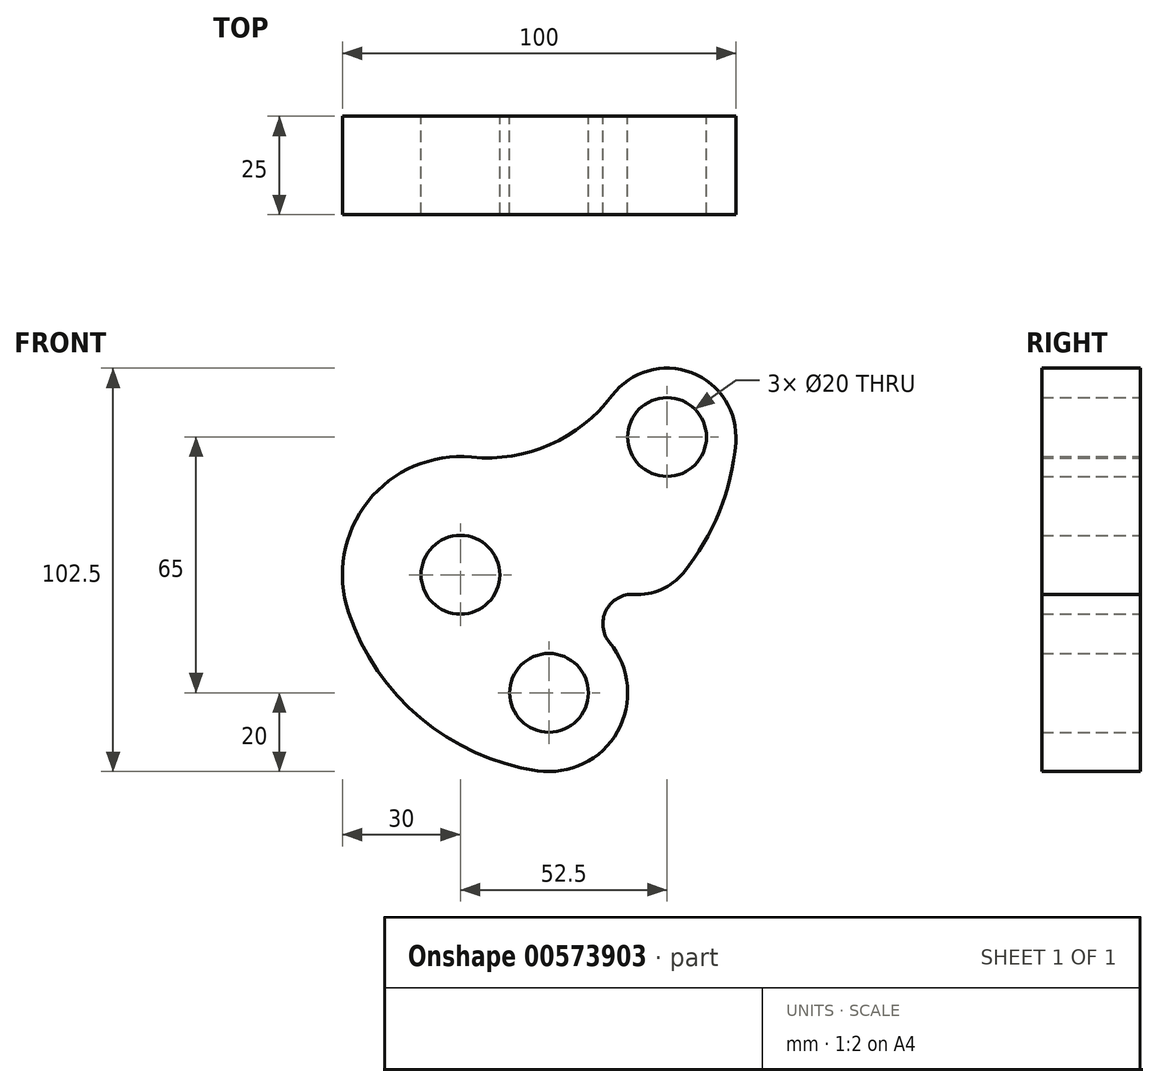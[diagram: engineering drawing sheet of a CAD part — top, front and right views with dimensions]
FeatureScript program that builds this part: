
annotation { "Feature Type Name" : "Feature", "Feature Type Description" : "" }
export const myFeature = defineFeature(function(context is Context, id is Id, definition is map)
    precondition{}
    {
        {
            var Q0;
            Q0=qCreatedBy(makeId("Front.planeOp"),FACE);
            var sketch = newSketch(context, id + "F0", { "sketchPlane" : qUnion([Q0])});
            skArc(sketch, "E0", {"start": v(69.94, 33.58) * mm, "mid": v(58.74, 51.35) * mm, "end": v(38.54, 45.56) * mm});
            skArc(sketch, "E1", {"start": v(2.85, 29.86) * mm, "mid": v(-23.5, 18.65) * mm, "end": v(-28.44, -9.56) * mm});
            skArc(sketch, "E2", {"start": v(19.53, -49.78) * mm, "mid": v(39.91, -39.83) * mm, "end": v(37.9, -17.24) * mm});
            skArc(sketch, "E3", {"start": v(2.85, 29.86) * mm, "mid": v(22.74, 33.07) * mm, "end": v(38.54, 45.56) * mm});
            skArc(sketch, "E4", {"start": v(-28.44, -9.56) * mm, "mid": v(-10.11, -36.42) * mm, "end": v(19.53, -49.78) * mm});
            skArc(sketch, "E5", {"start": v(44.12, -4.97) * mm, "mid": v(51.03, -3.73) * mm, "end": v(56.62, 0.51) * mm});
            skArc(sketch, "E6", {"start": v(56.62, 0.51) * mm, "mid": v(65.8, 16.03) * mm, "end": v(69.94, 33.58) * mm});
            skArc(sketch, "E7", {"start": v(44.12, -4.97) * mm, "mid": v(37, -9.07) * mm, "end": v(37.9, -17.24) * mm});
            skCircle(sketch, "E8", {"center": v(52.5, 35) * mm, "radius": 10 * mm});
            skCircle(sketch, "E9", {"center": v(0, 0) * mm, "radius": 10 * mm});
            skCircle(sketch, "E10", {"center": v(22.5, -30) * mm, "radius": 10 * mm});
            skSolve(sketch);
        }
        {
            var Q0;
            Q0=makeQuery(id+"F0.imprint","IMPRINT",FACE,{"disambiguationData":[TD([[makeQuery(id+"F0.imprint","IMPRINT",EDGE,{"derivedFrom":sQuery(id+"F0.wireOp",EDGE,"E0")}),1.0]])]});
            extrude(context, id + "F1", {"entities" : qUnion([Q0]), "depth" : 25 * mm, "offsetDistance" : 25 * mm});
        }
    });
